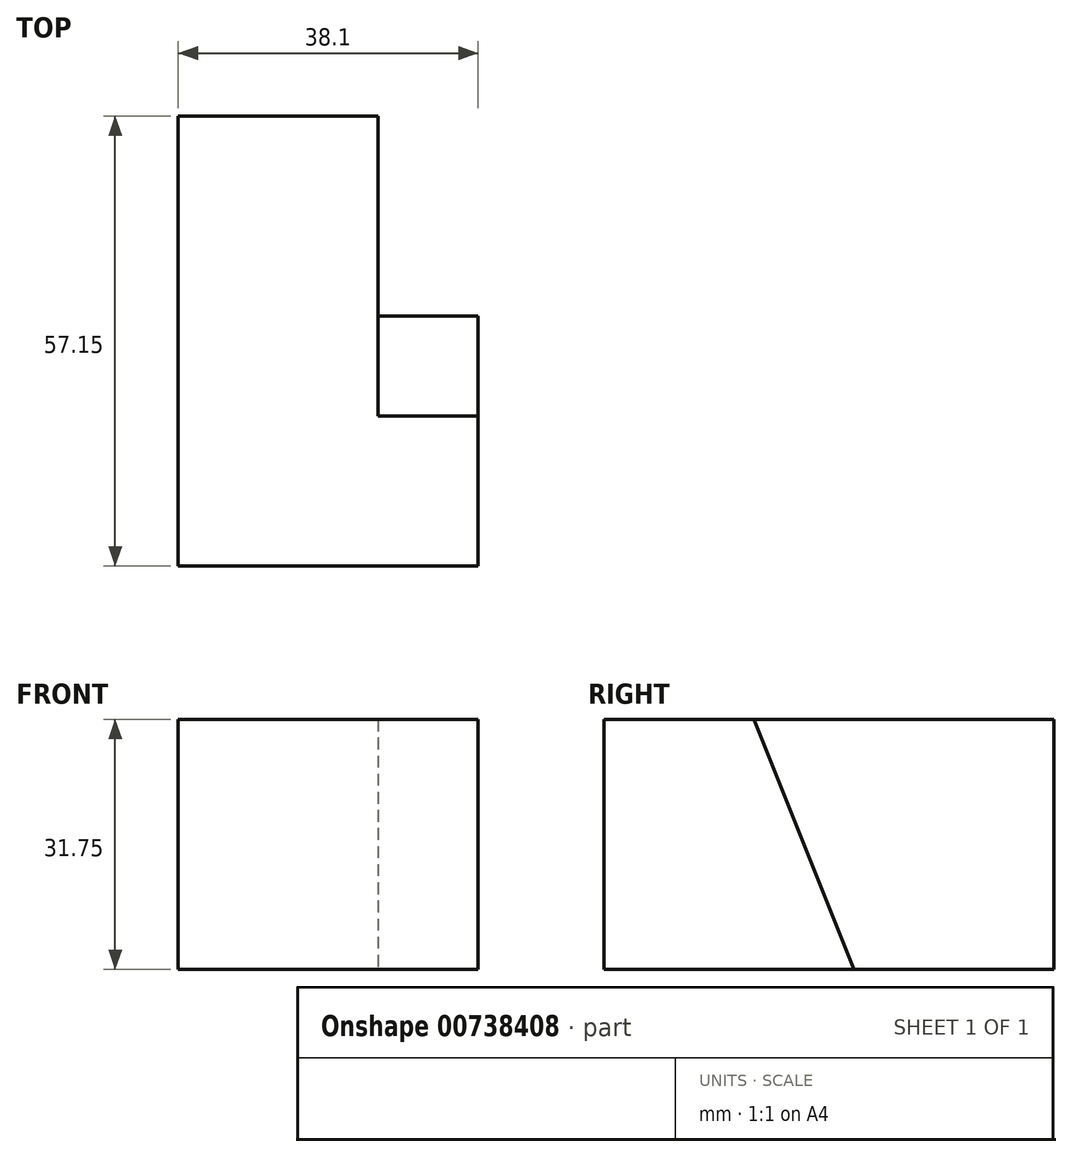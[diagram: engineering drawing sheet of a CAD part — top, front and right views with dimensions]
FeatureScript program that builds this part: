
annotation { "Feature Type Name" : "Feature", "Feature Type Description" : "" }
export const myFeature = defineFeature(function(context is Context, id is Id, definition is map)
    precondition{}
    {
        {
            var Q0;
            Q0=qCreatedBy(makeId("Top.planeOp"),FACE);
            var sketch = newSketch(context, id + "F0", { "sketchPlane" : qUnion([Q0])});
            skLineSegment(sketch, "E0.bottom", {"start": v(0, 0) * mm, "end": v(38.1, 0) * mm});
            skLineSegment(sketch, "E0.top", {"start": v(0, 57.15) * mm, "end": v(38.1, 57.15) * mm});
            skLineSegment(sketch, "E0.left", {"start": v(0, 0) * mm, "end": v(0, 57.15) * mm});
            skLineSegment(sketch, "E0.right", {"start": v(38.1, 0) * mm, "end": v(38.1, 57.15) * mm});
            skSolve(sketch);
        }
        {
            var Q0;
            Q0=makeQuery(id+"F0.imprint","IMPRINT",FACE,{"disambiguationData":[TD([[makeQuery(id+"F0.imprint","IMPRINT",EDGE,{"derivedFrom":sQuery(id+"F0.wireOp",EDGE,"E0.bottom")}),1.0]])]});
            extrude(context, id + "F1", {"entities" : qUnion([Q0]), "depth" : 31.75 * mm, "offsetDistance" : 25.4 * mm});
        }
        {
            var Q0;
            Q0=makeQuery(id+"F1.opExtrude","SWEPT_FACE",FACE,{"disambiguationData":[OSD([sQuery(id+"F0.wireOp",EDGE,"E0.right")])]});
            var sketch = newSketch(context, id + "F2", { "sketchPlane" : qUnion([Q0])});
            skLineSegment(sketch, "E1", {"start": v(19.05, 31.75) * mm, "end": v(31.75, 0) * mm});
            skLineSegment(sketch, "E2", {"start": v(31.75, 0) * mm, "end": v(57.15, 0) * mm});
            skLineSegment(sketch, "E3", {"start": v(57.15, 0) * mm, "end": v(57.15, 31.75) * mm});
            skLineSegment(sketch, "E4", {"start": v(57.15, 31.75) * mm, "end": v(19.05, 31.75) * mm});
            skSolve(sketch);
        }
        {
            var Q0;
            Q0 = qSketchRegion(id + "F2", true);
            extrude(context, id + "F3", {"entities" : qUnion([Q0]), "operationType" : NewBodyOperationType.REMOVE, "oppositeDirection" : true, "depth" : 12.7 * mm, "offsetDistance" : 25.4 * mm});
        }
    });
